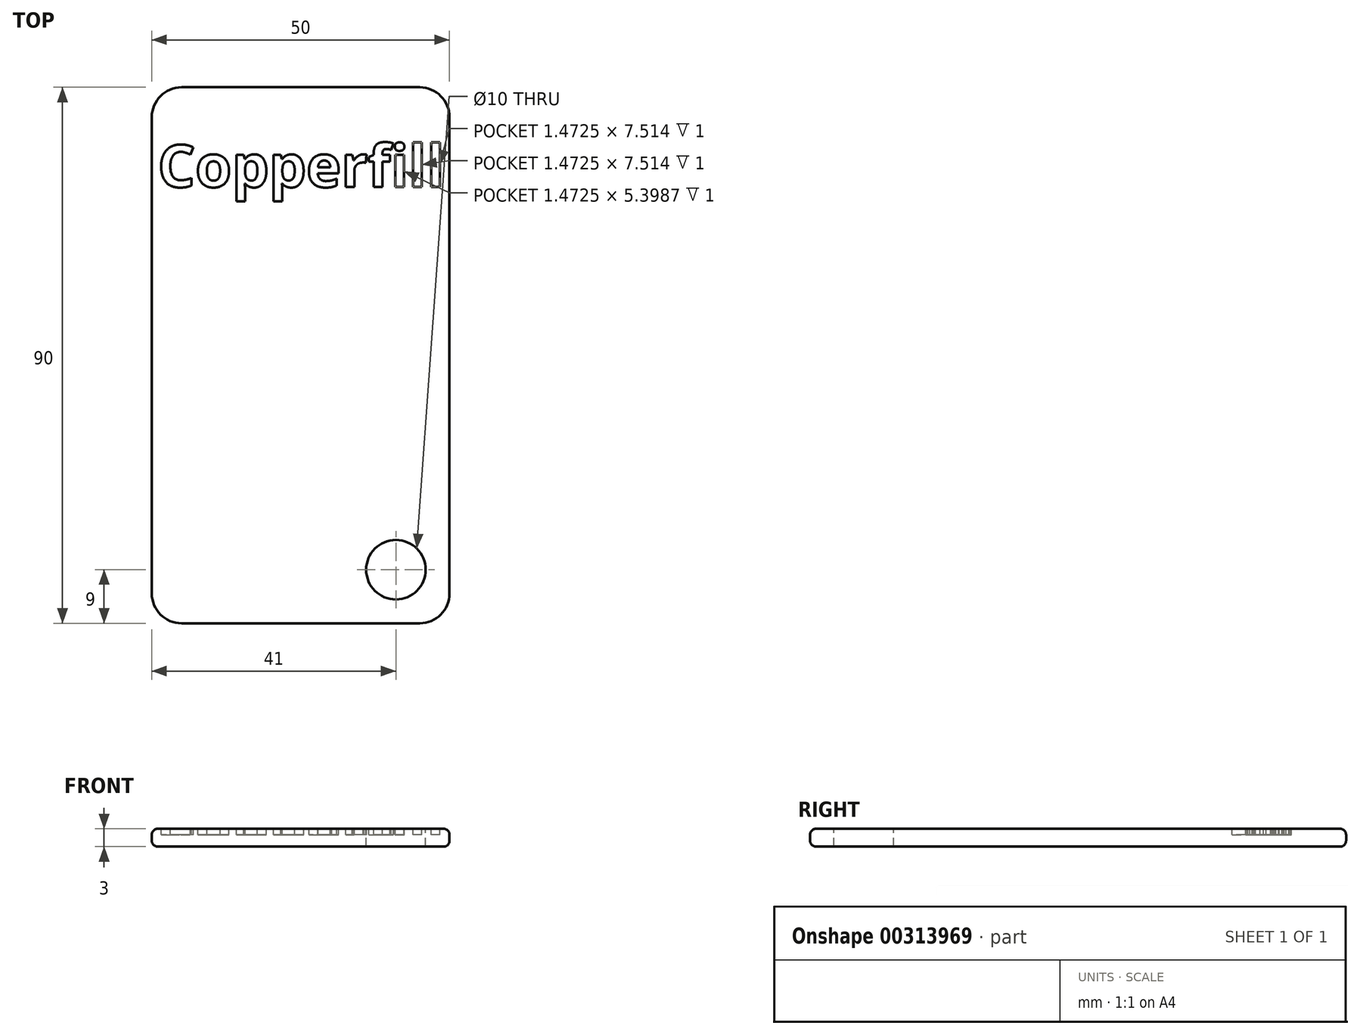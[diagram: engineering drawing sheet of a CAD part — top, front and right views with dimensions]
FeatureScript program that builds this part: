
annotation { "Feature Type Name" : "Feature", "Feature Type Description" : "" }
export const myFeature = defineFeature(function(context is Context, id is Id, definition is map)
    precondition{}
    {
        {
            var Q0;
            Q0=qCreatedBy(makeId("Top.planeOp"),FACE);
            var sketch = newSketch(context, id + "F0", { "sketchPlane" : qUnion([Q0])});
            skLineSegment(sketch, "E0.bottom", {"start": v(-45, 25) * mm, "end": v(45, 25) * mm});
            skLineSegment(sketch, "E0.top", {"start": v(-45, -25) * mm, "end": v(45, -25) * mm});
            skLineSegment(sketch, "E0.left", {"start": v(-45, 25) * mm, "end": v(-45, -25) * mm});
            skLineSegment(sketch, "E0.right", {"start": v(45, 25) * mm, "end": v(45, -25) * mm});
            skLineSegment(sketch, "E1", {"start": v(-45, 25) * mm, "end": v(45, -25) * mm, "construction": true});
            skSolve(sketch);
        }
        {
            var Q0;
            Q0=makeQuery(id+"F0.imprint","IMPRINT",FACE,{"disambiguationData":[TD([[makeQuery(id+"F0.imprint","IMPRINT",EDGE,{"derivedFrom":sQuery(id+"F0.wireOp",EDGE,"E0.bottom")}),-1.0]])]});
            extrude(context, id + "F1", {"entities" : qUnion([Q0]), "depth" : 3 * mm});
        }
        {
            var Q0;
            Q0=makeQuery(id+"F1.opExtrude","CAP_FACE",FACE,{"disambiguationData":[OSD([sQuery(id+"F0.wireOp",EDGE,"E0.bottom"),sQuery(id+"F0.wireOp",EDGE,"E0.top"),sQuery(id+"F0.wireOp",EDGE,"E0.left"),sQuery(id+"F0.wireOp",EDGE,"E0.right")])],"isStart":false});
            var Q1;
            Q1=makeQuery(id+"F1.opExtrude","CAP_FACE",FACE,{"disambiguationData":[OSD([sQuery(id+"F0.wireOp",EDGE,"E0.bottom"),sQuery(id+"F0.wireOp",EDGE,"E0.top"),sQuery(id+"F0.wireOp",EDGE,"E0.left"),sQuery(id+"F0.wireOp",EDGE,"E0.right")])],"isStart":true});
            fillet(context, id + "F2", {"entities" : qUnion([Q0, Q1]), "radius" : 1 * mm, "tangentPropagation" : true, "allowEdgeOverflow" : false});
        }
        {
            var Q0;
            Q0=makeQuery(id+"F1.opExtrude","SWEPT_EDGE",EDGE,{"disambiguationData":[OSD([sQuery(id+"F0.wireOp",EDGE,"E0.top"),sQuery(id+"F0.wireOp",EDGE,"E0.right")])]});
            var Q1;
            Q1=makeQuery(id+"F1.opExtrude","SWEPT_EDGE",EDGE,{"disambiguationData":[OSD([sQuery(id+"F0.wireOp",EDGE,"E0.bottom"),sQuery(id+"F0.wireOp",EDGE,"E0.right")])]});
            var Q2;
            Q2=makeQuery(id+"F1.opExtrude","SWEPT_EDGE",EDGE,{"disambiguationData":[OSD([sQuery(id+"F0.wireOp",EDGE,"E0.bottom"),sQuery(id+"F0.wireOp",EDGE,"E0.left")])]});
            var Q3;
            Q3=makeQuery(id+"F1.opExtrude","SWEPT_EDGE",EDGE,{"disambiguationData":[OSD([sQuery(id+"F0.wireOp",EDGE,"E0.top"),sQuery(id+"F0.wireOp",EDGE,"E0.left")])]});
            fillet(context, id + "F3", {"entities" : qUnion([Q0, Q1, Q2, Q3]), "radius" : 5 * mm, "tangentPropagation" : true, "allowEdgeOverflow" : false});
        }
        {
            var Q0;
            Q0=qCreatedBy(makeId("Right.planeOp"),FACE);
            var sketch = newSketch(context, id + "F4", { "sketchPlane" : qUnion([Q0])});
            skLineSegment(sketch, "E2", {"start": v(0, 0) * mm, "end": v(0, 32.9) * mm});
            skSolve(sketch);
        }
        {
            var Q0;
            Q0=makeQuery(id+"F1.opExtrude","SWEPT_BODY",BODY,{"disambiguationData":[OSD([sQuery(id+"F0.wireOp",EDGE,"E0.bottom"),sQuery(id+"F0.wireOp",EDGE,"E0.top"),sQuery(id+"F0.wireOp",EDGE,"E0.left"),sQuery(id+"F0.wireOp",EDGE,"E0.right")])]});
            var Q1;
            Q1=sQuery(id+"F4.wireOp",EDGE,"E2");
            transform(context, id + "F5", {"entities" : qUnion([Q0]), "transformType" : TransformType.ROTATION, "transformAxis" : qUnion([Q1]), "angle" : 90 * degree, "makeCopy" : false});
        }
        {
            var Q0;
            Q0=makeQuery(id+"F1.opExtrude","CAP_FACE",FACE,{"disambiguationData":[OSD([sQuery(id+"F0.wireOp",EDGE,"E0.bottom"),sQuery(id+"F0.wireOp",EDGE,"E0.top"),sQuery(id+"F0.wireOp",EDGE,"E0.left"),sQuery(id+"F0.wireOp",EDGE,"E0.right")])],"isStart":false});
            var sketch = newSketch(context, id + "F6", { "sketchPlane" : qUnion([Q0])});
            skText(sketch, "E3", { "text": "Copperfill", "fontName": "OpenSans-Bold.ttf"});
            const initialGuessF6  = {"E3": [-0.024, 0.02825, 1, 0, 0.00712]};
            skSetInitialGuess(sketch, initialGuessF6);
            skSolve(sketch);
        }
        {
            var Q0;
            Q0=qSketchRegion(id+"F6",true);
            extrude(context, id + "F7", {"entities" : qUnion([Q0]), "operationType" : NewBodyOperationType.REMOVE, "oppositeDirection" : true, "depth" : 1 * mm});
        }
        {
            var Q0;
            {var subQ0=sQuery(id+"F0.wireOp",EDGE,"E0.left");var subQ2=sQuery(id+"F0.wireOp",EDGE,"E0.bottom");var subQ4=sQuery(id+"F0.wireOp",EDGE,"E0.right");var subQ6=sQuery(id+"F0.wireOp",EDGE,"E0.top");Q0=makeQuery(id+"F7.boolean.opBoolean","SPLIT",FACE,{"disambiguationData":[TD([makeQuery(id+"F7.opExtrude","SWEPT_FACE",FACE,{"disambiguationData":[OSD([sQuery(id+"F6.wireOp",EDGE,"E3.sketch_text.stroke-0")])]})])],"derivedFrom":makeQuery(id+"F1.opExtrude","CAP_FACE",FACE,{"disambiguationData":[OSD([subQ2,subQ6,subQ0,subQ4])],"isStart":false})});}
            var sketch = newSketch(context, id + "F8", { "sketchPlane" : qUnion([Q0])});
            skCircle(sketch, "E4", {"center": v(16, -36) * mm, "radius": 5 * mm});
            skSolve(sketch);
        }
        {
            var Q0;
            Q0=qSketchRegion(id+"F8",true);
            extrude(context, id + "F9", {"entities" : qUnion([Q0]), "operationType" : NewBodyOperationType.REMOVE, "oppositeDirection" : true, "depth" : 3 * mm});
        }
    });
